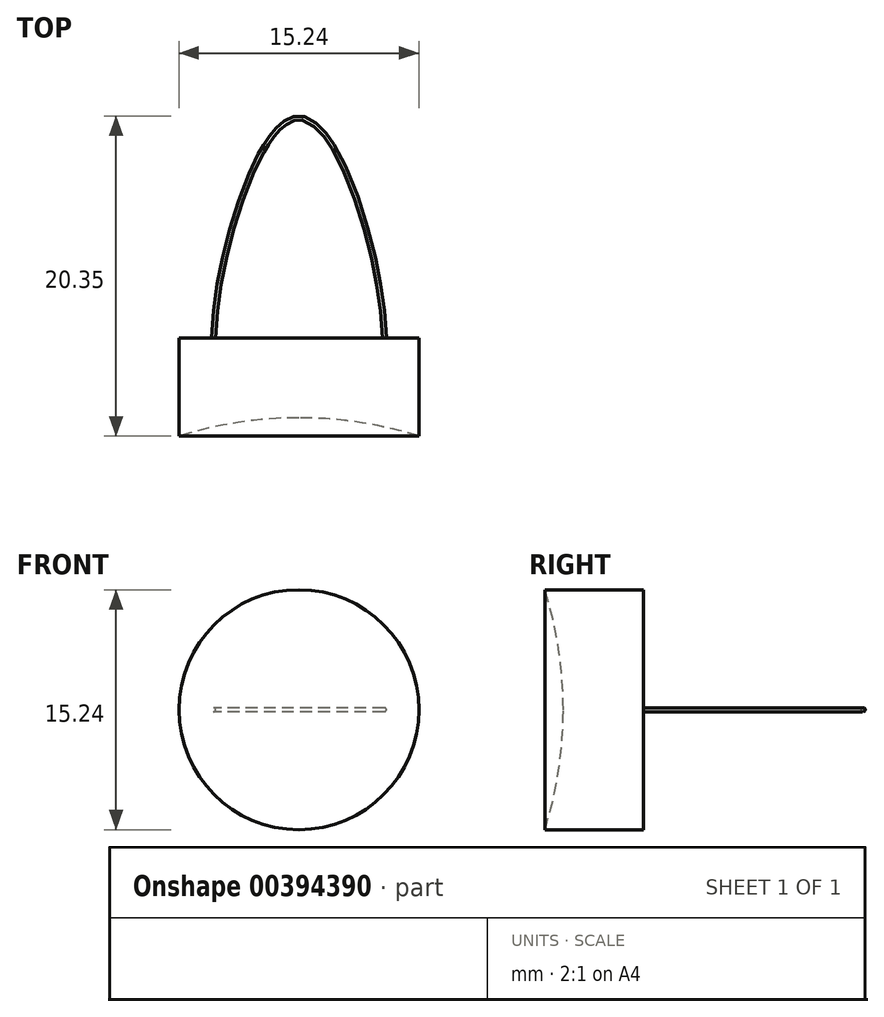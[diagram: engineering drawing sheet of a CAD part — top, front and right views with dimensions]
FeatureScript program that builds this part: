
annotation { "Feature Type Name" : "Feature", "Feature Type Description" : "" }
export const myFeature = defineFeature(function(context is Context, id is Id, definition is map)
    precondition{}
    {
        {
            var Q0;
            Q0=qCreatedBy(makeId("Top.planeOp"),FACE);
            var sketch = newSketch(context, id + "F0", { "sketchPlane" : qUnion([Q0])});
            skArc(sketch, "E0", {"start": v(0, 25.4) * mm, "mid": v(25.4, 0) * mm, "end": v(0, -25.4) * mm});
            skLineSegment(sketch, "E1", {"start": v(0, 25.4) * mm, "end": v(0, 0) * mm});
            skLineSegment(sketch, "E2", {"start": v(0, 0) * mm, "end": v(0, -25.4) * mm});
            skLineSegment(sketch, "E3", {"start": v(7.62, 24.23) * mm, "end": v(7.62, 30.48) * mm});
            skLineSegment(sketch, "E4", {"start": v(7.62, 30.48) * mm, "end": v(0, 30.48) * mm});
            skLineSegment(sketch, "E5", {"start": v(0, 30.48) * mm, "end": v(0, 25.4) * mm});
            skSolve(sketch);
        }
        {
            var Q0;
            Q0=makeQuery(id+"F0.imprint","IMPRINT",FACE,{"disambiguationData":[TD([[makeQuery(id+"F0.imprint","IMPRINT",EDGE,{"derivedFrom":sQuery(id+"F0.wireOp",EDGE,"E0")}),-1.0]])]});
            var Q1;
            {var subQ2=sQuery(id+"F0.wireOp",EDGE,"E3");Q1=makeQuery(id+"F0.imprint","IMPRINT",FACE,{"disambiguationData":[TD([[makeQuery(id+"F0.imprint","IMPRINT",EDGE,{"derivedFrom":subQ2}),1.0]])]});}
            var Q2;
            Q2=sQuery(id+"F0.wireOp",EDGE,"E2");
            revolve(context, id + "F1", {"entities" : qUnion([Q0, Q1]), "axis" : qUnion([Q2]), "revolveType" : RevolveType.FULL});
        }
        {
            var Q0;
            Q0=qCreatedBy(makeId("Top.planeOp"),FACE);
            var sketch = newSketch(context, id + "F2", { "sketchPlane" : qUnion([Q0])});
            skLineSegment(sketch, "E6", {"start": v(0, 0) * mm, "end": v(0, 27.94) * mm});
            skLineSegment(sketch, "E7", {"start": v(0, 27.94) * mm, "end": v(5.08, 27.94) * mm});
            skLineSegment(sketch, "E8", {"start": v(0, 27.94) * mm, "end": v(-5.08, 27.94) * mm});
            skLineSegment(sketch, "E9", {"start": v(0, 0) * mm, "end": v(0, 44.45) * mm});
            skFitSpline(sketch, "E10", {"points": [v(0, 44.45) * mm, v(-5.08, 27.94) * mm, v(0, 27.94) * mm, v(5.08, 27.94) * mm, v(0, 44.45) * mm]});
            skSolve(sketch);
        }
        {
            var Q0;
            Q0=qCreatedBy(makeId("Right.planeOp"),FACE);
            var sketch = newSketch(context, id + "F3", { "sketchPlane" : qUnion([Q0])});
            skPoint(sketch, "E11.0", {"position": v(44.45, 0) * mm});
            skCircle(sketch, "E12", {"center": v(44.45, 0) * mm, "radius": 0.13 * mm});
            skSolve(sketch);
        }
        {
            var Q0;
            Q0=makeQuery(id+"F3.imprint","IMPRINT",FACE,{"disambiguationData":[TD([[makeQuery(id+"F3.imprint","IMPRINT",EDGE,{"derivedFrom":sQuery(id+"F3.wireOp",EDGE,"E12")}),1.0]])]});
            var Q1;
            Q1=sQuery(id+"F2.wireOp",EDGE,"E10");
            sweep(context, id + "F4", {"operationType" : NewBodyOperationType.ADD, "profiles" : qUnion([Q0]), "path" : qUnion([Q1])});
        }
    });
